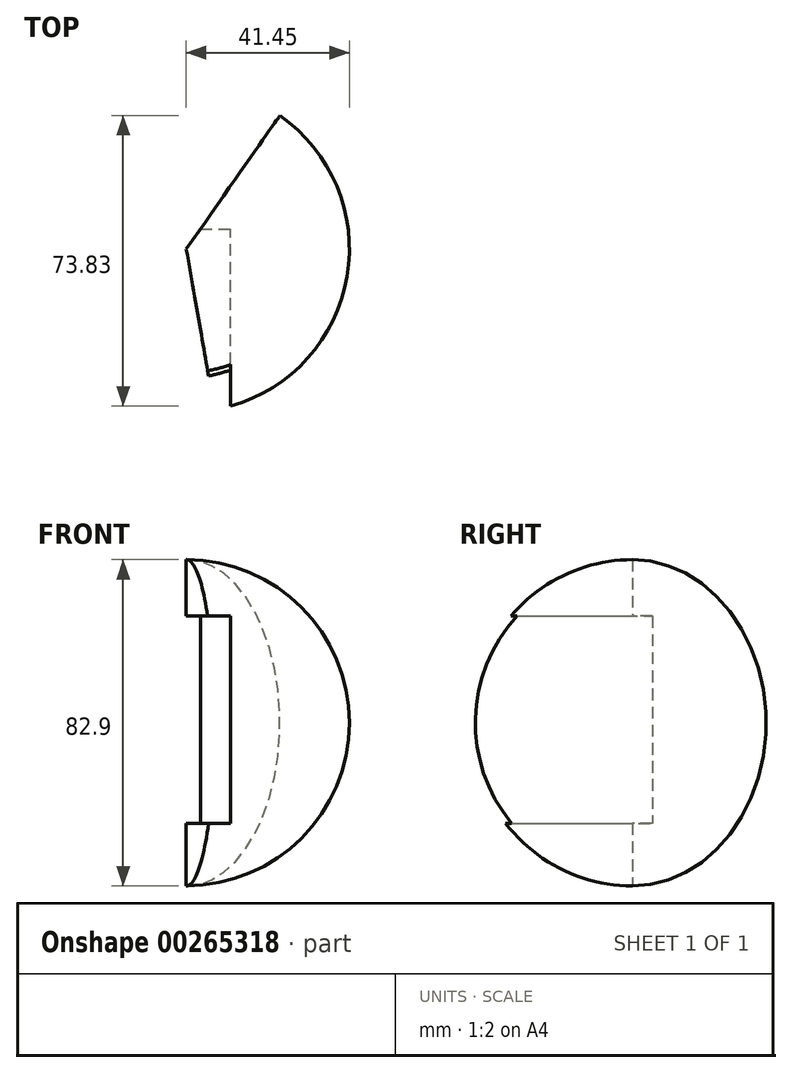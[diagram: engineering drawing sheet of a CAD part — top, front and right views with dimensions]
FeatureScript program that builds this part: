
annotation { "Feature Type Name" : "Feature", "Feature Type Description" : "" }
export const myFeature = defineFeature(function(context is Context, id is Id, definition is map)
    precondition{}
    {
        {
            var Q0;
            Q0=qCreatedBy(makeId("Front.planeOp"),FACE);
            var sketch = newSketch(context, id + "F0", { "sketchPlane" : qUnion([Q0])});
            skCircle(sketch, "E0", {"center": v(-51.17, 19.66) * mm, "radius": 41.45 * mm});
            skLineSegment(sketch, "E1", {"start": v(-51.17, 61.1) * mm, "end": v(-51.17, -21.8) * mm});
            skSolve(sketch);
        }
        {
            var Q0;
            {var subQ0=sQuery(id+"F0.wireOp",EDGE,"E1");Q0=makeQuery(id+"F0.imprint","IMPRINT",FACE,{"disambiguationData":[TD([[makeQuery(id+"F0.imprint","IMPRINT",EDGE,{"derivedFrom":subQ0}),1.0]])]});}
            var Q1;
            Q1=sQuery(id+"F0.wireOp",EDGE,"E1");
            revolve(context, id + "F1", {"entities" : qUnion([Q0]), "axis" : qUnion([Q1]), "revolveType" : RevolveType.TWO_DIRECTIONS, "angle" : 80 * degree, "angleBack" : 305 * degree});
        }
        {
            var Q0;
            Q0=qCreatedBy(makeId("Front.planeOp"),FACE);
            var sketch = newSketch(context, id + "F2", { "sketchPlane" : qUnion([Q0])});
            skLineSegment(sketch, "E2.bottom", {"start": v(-75.28, -5.84) * mm, "end": v(-39.88, -5.84) * mm});
            skLineSegment(sketch, "E2.top", {"start": v(-75.28, 46.75) * mm, "end": v(-39.88, 46.75) * mm});
            skLineSegment(sketch, "E2.left", {"start": v(-75.28, -5.84) * mm, "end": v(-75.28, 46.75) * mm});
            skLineSegment(sketch, "E2.right", {"start": v(-39.88, -5.84) * mm, "end": v(-39.88, 46.75) * mm});
            skSolve(sketch);
        }
        {
            var Q0;
            Q0=makeQuery(id+"F2.imprint","IMPRINT",FACE,{"disambiguationData":[TD([[makeQuery(id+"F2.imprint","IMPRINT",EDGE,{"derivedFrom":sQuery(id+"F2.wireOp",EDGE,"E2.bottom")}),1.0]])]});
            extrude(context, id + "F3", {"entities" : qUnion([Q0]), "operationType" : NewBodyOperationType.REMOVE, "depth" : 91 * mm, "hasSecondDirection" : true, "secondDirectionOppositeDirection" : true, "secondDirectionDepth" : 5.1 * mm});
        }
    });
